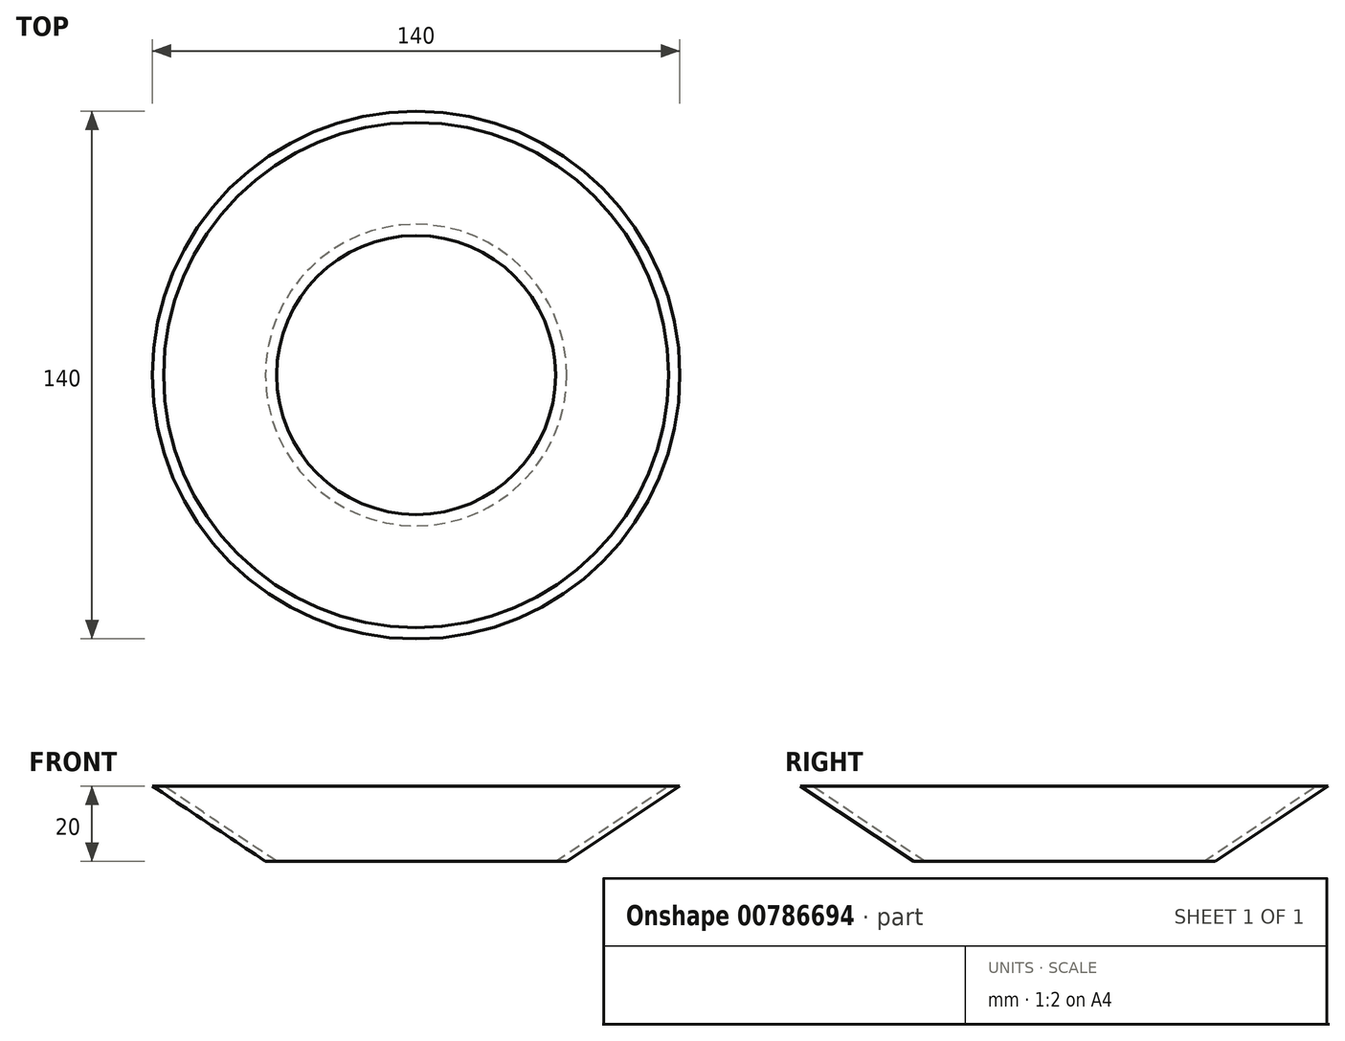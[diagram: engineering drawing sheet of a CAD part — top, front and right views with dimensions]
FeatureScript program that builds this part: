
annotation { "Feature Type Name" : "Feature", "Feature Type Description" : "" }
export const myFeature = defineFeature(function(context is Context, id is Id, definition is map)
    precondition{}
    {
        {
            var Q0;
            Q0=qCreatedBy(makeId("Front.planeOp"),FACE);
            var sketch = newSketch(context, id + "F0", { "sketchPlane" : qUnion([Q0])});
            skLineSegment(sketch, "E0", {"start": v(-70, 10) * mm, "end": v(-40, -10) * mm});
            skLineSegment(sketch, "E1", {"start": v(-40, -10) * mm, "end": v(-37, -10) * mm});
            skLineSegment(sketch, "E2", {"start": v(-37, -10) * mm, "end": v(-67, 10) * mm});
            skLineSegment(sketch, "E3", {"start": v(-67, 10) * mm, "end": v(-70, 10) * mm});
            skLineSegment(sketch, "E4", {"start": v(0, 0) * mm, "end": v(0, 37.4) * mm, "construction": true});
            skSolve(sketch);
        }
        {
            var Q0;
            Q0=makeQuery(id+"F0.imprint","IMPRINT",FACE,{"disambiguationData":[TD([[makeQuery(id+"F0.imprint","IMPRINT",EDGE,{"derivedFrom":sQuery(id+"F0.wireOp",EDGE,"E0")}),1.0]])]});
            var Q1;
            Q1=sQuery(id+"F0.wireOp",EDGE,"E4");
            revolve(context, id + "F1", {"surfaceOperationType" : NewSurfaceOperationType.NEW, "entities" : qUnion([Q0]), "axis" : qUnion([Q1]), "revolveType" : RevolveType.FULL});
        }
    });
